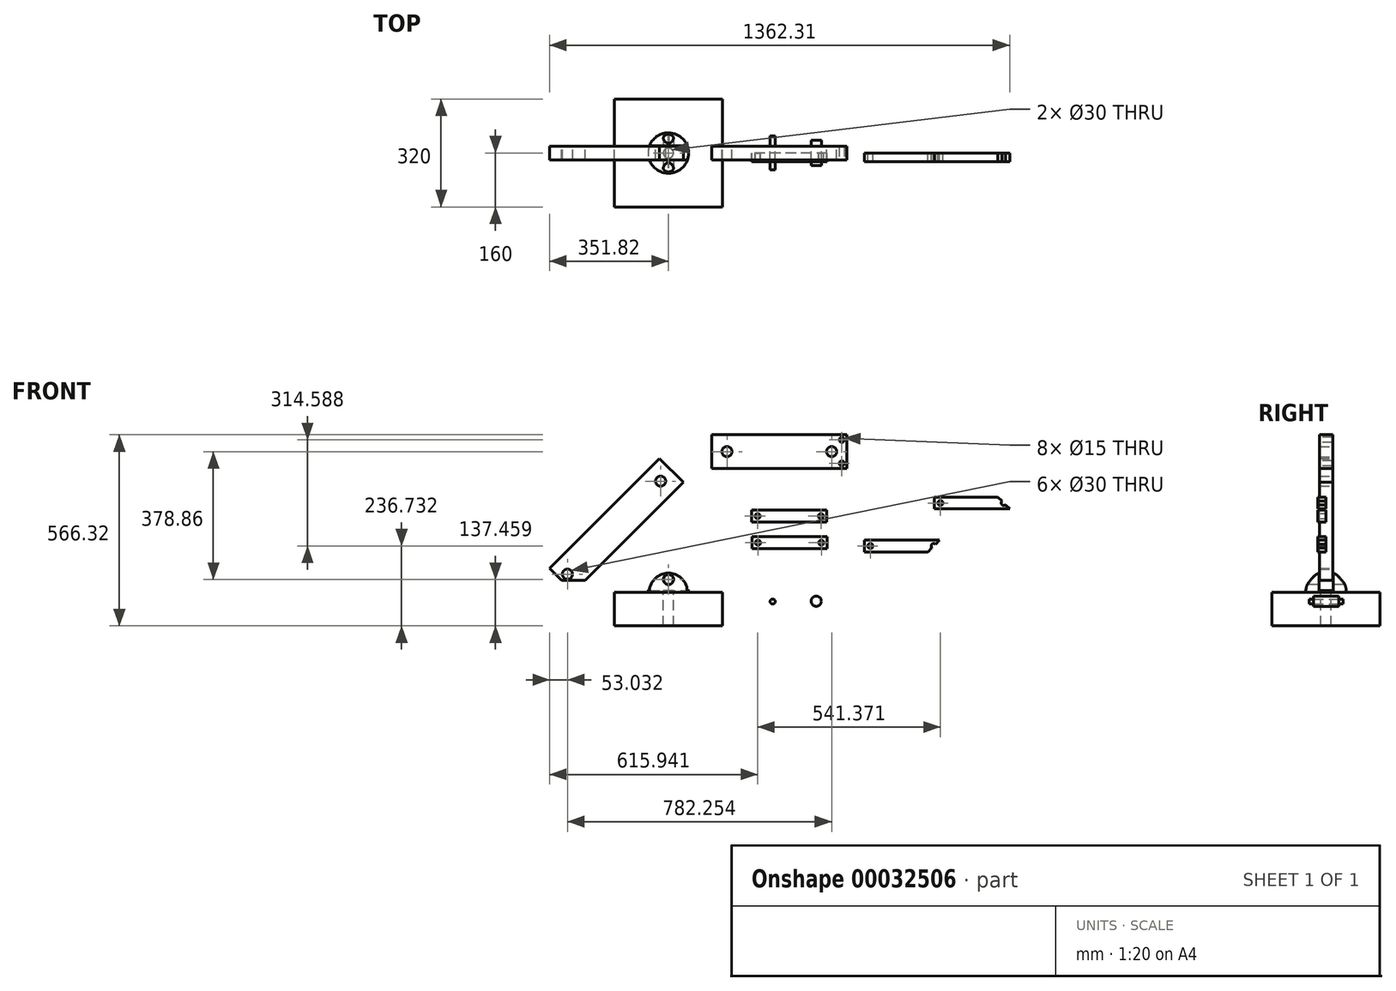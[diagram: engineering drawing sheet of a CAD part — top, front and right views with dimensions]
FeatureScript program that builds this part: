
annotation { "Feature Type Name" : "Feature", "Feature Type Description" : "" }
export const myFeature = defineFeature(function(context is Context, id is Id, definition is map)
    precondition{}
    {
        {
            var Q0;
            Q0=qCreatedBy(makeId("Front.planeOp"),FACE);
            var sketch = newSketch(context, id + "F0", { "sketchPlane" : qUnion([Q0])});
            skLineSegment(sketch, "E0.rect.bottom", {"start": v(-160, 50) * mm, "end": v(160, 50) * mm});
            skLineSegment(sketch, "E0.rect.top", {"start": v(-160, -50) * mm, "end": v(160, -50) * mm});
            skLineSegment(sketch, "E0.rect.left", {"start": v(-160, 50) * mm, "end": v(-160, -50) * mm});
            skLineSegment(sketch, "E0.rect.right", {"start": v(160, 50) * mm, "end": v(160, -50) * mm});
            skPoint(sketch, "E0.rect.middle", {"position": v(0, 0) * mm});
            skLineSegment(sketch, "E1", {"start": v(-351.82, 120.71) * mm, "end": v(-26.55, 445.98) * mm});
            skLineSegment(sketch, "E2", {"start": v(-26.55, 445.98) * mm, "end": v(44.16, 375.27) * mm});
            skLineSegment(sketch, "E3", {"start": v(-351.82, 120.71) * mm, "end": v(-281.11, 50) * mm});
            skLineSegment(sketch, "E4", {"start": v(-281.11, 50) * mm, "end": v(44.16, 375.27) * mm});
            skCircle(sketch, "E5", {"center": v(-298.79, 103.03) * mm, "radius": 15 * mm});
            skLineSegment(sketch, "E6.bottom", {"start": v(128.47, 416.32) * mm, "end": v(528.47, 416.32) * mm});
            skLineSegment(sketch, "E6.top", {"start": v(128.47, 516.32) * mm, "end": v(528.47, 516.32) * mm});
            skLineSegment(sketch, "E6.left", {"start": v(128.47, 416.32) * mm, "end": v(128.47, 516.32) * mm});
            skLineSegment(sketch, "E6.right", {"start": v(528.47, 416.32) * mm, "end": v(528.47, 516.32) * mm});
            skCircle(sketch, "E7", {"center": v(-23.02, 378.8) * mm, "radius": 15 * mm});
            skCircle(sketch, "E8", {"center": v(173.47, 466.32) * mm, "radius": 15 * mm});
            skCircle(sketch, "E9", {"center": v(483.47, 466.32) * mm, "radius": 15 * mm});
            skLineSegment(sketch, "E10", {"start": v(-316.47, 85.36) * mm, "end": v(-245.76, 85.36) * mm});
            skSolve(sketch);
        }
        {
            var Q0;
            Q0=makeQuery(id+"F0.imprint","IMPRINT",FACE,{"disambiguationData":[TD([[makeQuery(id+"F0.imprint","IMPRINT",EDGE,{"derivedFrom":sQuery(id+"F0.wireOp",EDGE,"E0.rect.bottom")}),-1.0]])]});
            extrude(context, id + "F1", {"entities" : qUnion([Q0]), "endBound" : BoundingType.SYMMETRIC, "depth" : 320 * mm});
        }
        {
            var Q0;
            Q0=makeQuery(id+"F0.imprint","IMPRINT",FACE,{"disambiguationData":[TD([[makeQuery(id+"F0.imprint","IMPRINT",EDGE,{"derivedFrom":sQuery(id+"F0.wireOp",EDGE,"E0.rect.bottom")}),-1.0]])]});
            var Q1;
            Q1=makeQuery(id+"F0.imprint","IMPRINT",FACE,{"disambiguationData":[TD([[makeQuery(id+"F0.imprint","IMPRINT",EDGE,{"derivedFrom":sQuery(id+"F0.wireOp",EDGE,"E6.bottom")}),1.0]])]});
            var Q2;
            {var subQ4=sQuery(id+"F0.wireOp",EDGE,"E1");Q2=makeQuery(id+"F0.imprint","IMPRINT",FACE,{"disambiguationData":[TD([[makeQuery(id+"F0.imprint","IMPRINT",EDGE,{"derivedFrom":subQ4}),-1.0]])]});}
            extrude(context, id + "F2", {"entities" : qUnion([Q0, Q1, Q2]), "operationType" : NewBodyOperationType.ADD, "endBound" : BoundingType.SYMMETRIC, "depth" : 40 * mm});
        }
        {
            var Q0;
            Q0=qCreatedBy(makeId("Right.planeOp"),FACE);
            var sketch = newSketch(context, id + "F3", { "sketchPlane" : qUnion([Q0])});
            skArc(sketch, "E11", {"start": v(60, 50.85) * mm, "mid": v(-0.12, 110) * mm, "end": v(-60, 50.6) * mm});
            skLineSegment(sketch, "E12", {"start": v(111.05, 50) * mm, "end": v(-104.71, 50) * mm, "construction": true});
            skLineSegment(sketch, "E13", {"start": v(60, 50.85) * mm, "end": v(-60, 50.6) * mm});
            skLineSegment(sketch, "E14.bottom", {"start": v(21, 50.77) * mm, "end": v(-21, 50.77) * mm});
            skSolve(sketch);
        }
        {
            var Q0;
            Q0 = qSketchRegion(id + "F3", true);
            var Q1;
            Q1=sQuery(id+"F3.wireOp",EDGE,"E12");
            revolve(context, id + "F4", {"entities" : qUnion([Q0]), "axis" : qUnion([Q1]), "revolveType" : RevolveType.SYMMETRIC, "angle" : 180 * degree});
        }
        {
            var Q0;
            Q0=qCreatedBy(makeId("Right.planeOp"),FACE);
            var sketch = newSketch(context, id + "F5", { "sketchPlane" : qUnion([Q0])});
            skLineSegment(sketch, "E15.bottom", {"start": v(21, 55) * mm, "end": v(-21, 55) * mm});
            skLineSegment(sketch, "E15.top", {"start": v(21, 127.52) * mm, "end": v(-21, 127.52) * mm});
            skLineSegment(sketch, "E15.left", {"start": v(21, 55) * mm, "end": v(21, 127.52) * mm});
            skLineSegment(sketch, "E15.right", {"start": v(-21, 55) * mm, "end": v(-21, 127.52) * mm});
            skSolve(sketch);
        }
        {
            var Q0;
            Q0 = qSketchRegion(id + "F5", true);
            extrude(context, id + "F6", {"entities" : qUnion([Q0]), "operationType" : NewBodyOperationType.REMOVE, "endBound" : BoundingType.SYMMETRIC, "oppositeDirection" : true, "depth" : 200 * mm});
        }
        {
            var Q0;
            Q0=makeQuery(id+"F6.boolean.opBoolean","COPY",FACE,{"derivedFrom":makeQuery(id+"F6.opExtrude","SWEPT_FACE",FACE,{"disambiguationData":[OSD([sQuery(id+"F5.wireOp",EDGE,"E15.bottom")])]})});
            var sketch = newSketch(context, id + "F7", { "sketchPlane" : qUnion([Q0])});
            skCircle(sketch, "E16", {"center": v(0, 0) * mm, "radius": 15 * mm});
            skSolve(sketch);
        }
        {
            var Q0;
            Q0 = qSketchRegion(id + "F7", true);
            extrude(context, id + "F8", {"entities" : qUnion([Q0]), "operationType" : NewBodyOperationType.REMOVE, "endBound" : BoundingType.THROUGH_ALL, "oppositeDirection" : true, "depth" : 25 * mm});
        }
        {
            var Q0;
            Q0=makeQuery(id+"F1.opExtrude","SWEPT_FACE",FACE,{"disambiguationData":[OSD([sQuery(id+"F0.wireOp",EDGE,"E0.rect.bottom")])]});
            var sketch = newSketch(context, id + "F9", { "sketchPlane" : qUnion([Q0])});
            skCircle(sketch, "E17", {"center": v(0, 0) * mm, "radius": 15 * mm});
            skSolve(sketch);
        }
        {
            var Q0;
            Q0=makeQuery(id+"F9.imprint","IMPRINT",FACE,{"disambiguationData":[TD([[makeQuery(id+"F9.imprint","IMPRINT",EDGE,{"derivedFrom":sQuery(id+"F9.wireOp",EDGE,"E17")}),1.0]])]});
            extrude(context, id + "F10", {"entities" : qUnion([Q0]), "operationType" : NewBodyOperationType.REMOVE, "oppositeDirection" : true, "depth" : 388.24 * mm});
        }
        {
            var Q0;
            Q0=makeQuery(id+"F6.boolean.opBoolean","COPY",FACE,{"derivedFrom":makeQuery(id+"F6.opExtrude","SWEPT_FACE",FACE,{"disambiguationData":[OSD([sQuery(id+"F5.wireOp",EDGE,"E15.left")])]})});
            var sketch = newSketch(context, id + "F11", { "sketchPlane" : qUnion([Q0])});
            skCircle(sketch, "E18", {"center": v(0, 87.46) * mm, "radius": 15 * mm});
            skSolve(sketch);
        }
        {
            var Q0;
            Q0 = qSketchRegion(id + "F11", true);
            extrude(context, id + "F12", {"entities" : qUnion([Q0]), "operationType" : NewBodyOperationType.REMOVE, "endBound" : BoundingType.SYMMETRIC, "oppositeDirection" : true, "depth" : 1076.07 * mm});
        }
        {
            var Q0;
            Q0=qCreatedBy(makeId("Front.planeOp"),FACE);
            var sketch = newSketch(context, id + "F13", { "sketchPlane" : qUnion([Q0])});
            skLineSegment(sketch, "E19.rect.bottom", {"start": v(469.12, 257.63) * mm, "end": v(246.62, 257.63) * mm});
            skLineSegment(sketch, "E19.rect.top", {"start": v(469.12, 292.63) * mm, "end": v(246.62, 292.63) * mm});
            skLineSegment(sketch, "E19.rect.left", {"start": v(469.12, 257.63) * mm, "end": v(469.12, 292.63) * mm});
            skLineSegment(sketch, "E19.rect.right", {"start": v(246.62, 257.63) * mm, "end": v(246.62, 292.63) * mm});
            skPoint(sketch, "E19.rect.middle", {"position": v(357.87, 275.13) * mm});
            skLineSegment(sketch, "E20.rect.bottom", {"start": v(470.28, 213.88) * mm, "end": v(247.78, 213.88) * mm});
            skLineSegment(sketch, "E20.rect.top", {"start": v(470.28, 178.88) * mm, "end": v(247.78, 178.88) * mm});
            skLineSegment(sketch, "E20.rect.left", {"start": v(470.28, 213.88) * mm, "end": v(470.28, 178.88) * mm});
            skLineSegment(sketch, "E20.rect.right", {"start": v(247.78, 213.88) * mm, "end": v(247.78, 178.88) * mm});
            skPoint(sketch, "E20.rect.middle", {"position": v(359.03, 196.38) * mm});
            skCircle(sketch, "E21", {"center": v(264.12, 275.13) * mm, "radius": 7.5 * mm});
            skCircle(sketch, "E22", {"center": v(265.28, 196.38) * mm, "radius": 7.5 * mm});
            skPoint(sketch, "E22.centerSnap0", {"position": v(247.78, 196.38) * mm});
            skCircle(sketch, "E23", {"center": v(451.62, 275.13) * mm, "radius": 7.5 * mm});
            skPoint(sketch, "E23.centerSnap0", {"position": v(469.12, 275.13) * mm});
            skCircle(sketch, "E24", {"center": v(452.78, 196.38) * mm, "radius": 7.5 * mm});
            skPoint(sketch, "E24.centerSnap0", {"position": v(470.28, 196.38) * mm});
            skLineSegment(sketch, "E25.rect.right", {"start": v(580.47, 169.23) * mm, "end": v(580.47, 204.23) * mm});
            skLineSegment(sketch, "E25.rect.top", {"start": v(802.97, 204.23) * mm, "end": v(580.47, 204.23) * mm});
            skCircle(sketch, "E26", {"center": v(785.47, 186.73) * mm, "radius": 7.5 * mm});
            skPoint(sketch, "E25.rect.middle", {"position": v(691.72, 186.73) * mm});
            skPoint(sketch, "E26.centerSnap0", {"position": v(802.97, 186.73) * mm});
            skLineSegment(sketch, "E25.rect.left", {"start": v(802.97, 169.23) * mm, "end": v(802.97, 204.23) * mm});
            skCircle(sketch, "E27", {"center": v(597.97, 186.73) * mm, "radius": 7.5 * mm});
            skLineSegment(sketch, "E25.rect.bottom", {"start": v(802.97, 169.23) * mm, "end": v(580.47, 169.23) * mm});
            skLineSegment(sketch, "E28.rect.right", {"start": v(788, 296.63) * mm, "end": v(788, 331.63) * mm});
            skLineSegment(sketch, "E28.rect.top", {"start": v(1010.5, 331.63) * mm, "end": v(788, 331.63) * mm});
            skCircle(sketch, "E29", {"center": v(993, 314.13) * mm, "radius": 7.5 * mm});
            skPoint(sketch, "E28.rect.middle", {"position": v(899.24, 314.13) * mm});
            skPoint(sketch, "E29.centerSnap0", {"position": v(1010.5, 314.13) * mm});
            skLineSegment(sketch, "E28.rect.left", {"start": v(1010.5, 296.63) * mm, "end": v(1010.5, 331.63) * mm});
            skCircle(sketch, "E30", {"center": v(805.5, 314.13) * mm, "radius": 7.5 * mm});
            skLineSegment(sketch, "E28.rect.bottom", {"start": v(1010.5, 296.63) * mm, "end": v(788, 296.63) * mm});
            skLineSegment(sketch, "E31", {"start": v(802.97, 204.23) * mm, "end": v(767.97, 169.23) * mm});
            skLineSegment(sketch, "E32", {"start": v(1010.5, 296.63) * mm, "end": v(975.5, 331.63) * mm});
            skSolve(sketch);
        }
        {
            var Q0;
            Q0=makeQuery(id+"F2.opExtrude","CAP_FACE",FACE,{"disambiguationData":[OSD([sQuery(id+"F0.wireOp",EDGE,"E6.bottom"),sQuery(id+"F0.wireOp",EDGE,"E6.top"),sQuery(id+"F0.wireOp",EDGE,"E6.left"),sQuery(id+"F0.wireOp",EDGE,"E6.right"),sQuery(id+"F0.wireOp",EDGE,"E8"),sQuery(id+"F0.wireOp",EDGE,"E9")])],"isStart":false});
            var sketch = newSketch(context, id + "F14", { "sketchPlane" : qUnion([Q0])});
            skCircle(sketch, "E33", {"center": v(513.47, 501.32) * mm, "radius": 7.5 * mm});
            skCircle(sketch, "E34", {"center": v(513.47, 431.32) * mm, "radius": 7.5 * mm});
            skSolve(sketch);
        }
        {
            var Q0;
            Q0 = qSketchRegion(id + "F14", true);
            extrude(context, id + "F15", {"entities" : qUnion([Q0]), "operationType" : NewBodyOperationType.REMOVE, "endBound" : BoundingType.THROUGH_ALL, "oppositeDirection" : true, "depth" : 25 * mm});
        }
        {
            var Q0;
            Q0=makeQuery(id+"F13.imprint","IMPRINT",FACE,{"disambiguationData":[TD([[makeQuery(id+"F13.imprint","IMPRINT",EDGE,{"derivedFrom":sQuery(id+"F13.wireOp",EDGE,"E19.rect.bottom")}),-1.0]])]});
            var Q1;
            Q1=makeQuery(id+"F13.imprint","IMPRINT",FACE,{"disambiguationData":[TD([[makeQuery(id+"F13.imprint","IMPRINT",EDGE,{"derivedFrom":sQuery(id+"F13.wireOp",EDGE,"E20.rect.bottom")}),1.0]])]});
            var Q2;
            {var subQ7=sQuery(id+"F13.wireOp",EDGE,"E25.rect.right");Q2=makeQuery(id+"F13.imprint","IMPRINT",FACE,{"disambiguationData":[TD([[makeQuery(id+"F13.imprint","IMPRINT",EDGE,{"derivedFrom":subQ7}),-1.0]])]});}
            var Q3;
            {var subQ7=sQuery(id+"F13.wireOp",EDGE,"E28.rect.right");Q3=makeQuery(id+"F13.imprint","IMPRINT",FACE,{"disambiguationData":[TD([[makeQuery(id+"F13.imprint","IMPRINT",EDGE,{"derivedFrom":subQ7}),-1.0]])]});}
            extrude(context, id + "F16", {"entities" : qUnion([Q0, Q1, Q2, Q3]), "depth" : 25 * mm});
        }
        {
            var Q0;
            Q0=qCreatedBy(makeId("Front.planeOp"),FACE);
            var sketch = newSketch(context, id + "F17", { "sketchPlane" : qUnion([Q0])});
            skCircle(sketch, "E35", {"center": v(437.87, 22.97) * mm, "radius": 15 * mm});
            skSolve(sketch);
        }
        {
            var Q0;
            Q0 = qSketchRegion(id + "F17", true);
            extrude(context, id + "F18", {"entities" : qUnion([Q0]), "endBound" : BoundingType.SYMMETRIC, "depth" : 75 * mm});
        }
        {
            var Q0;
            Q0=qCreatedBy(makeId("Front.planeOp"),FACE);
            var sketch = newSketch(context, id + "F19", { "sketchPlane" : qUnion([Q0])});
            skCircle(sketch, "E36", {"center": v(308.82, 22.07) * mm, "radius": 7.5 * mm});
            skSolve(sketch);
        }
        {
            var Q0;
            Q0 = qSketchRegion(id + "F19", true);
            extrude(context, id + "F20", {"entities" : qUnion([Q0]), "endBound" : BoundingType.SYMMETRIC, "depth" : 100 * mm});
        }
    });
